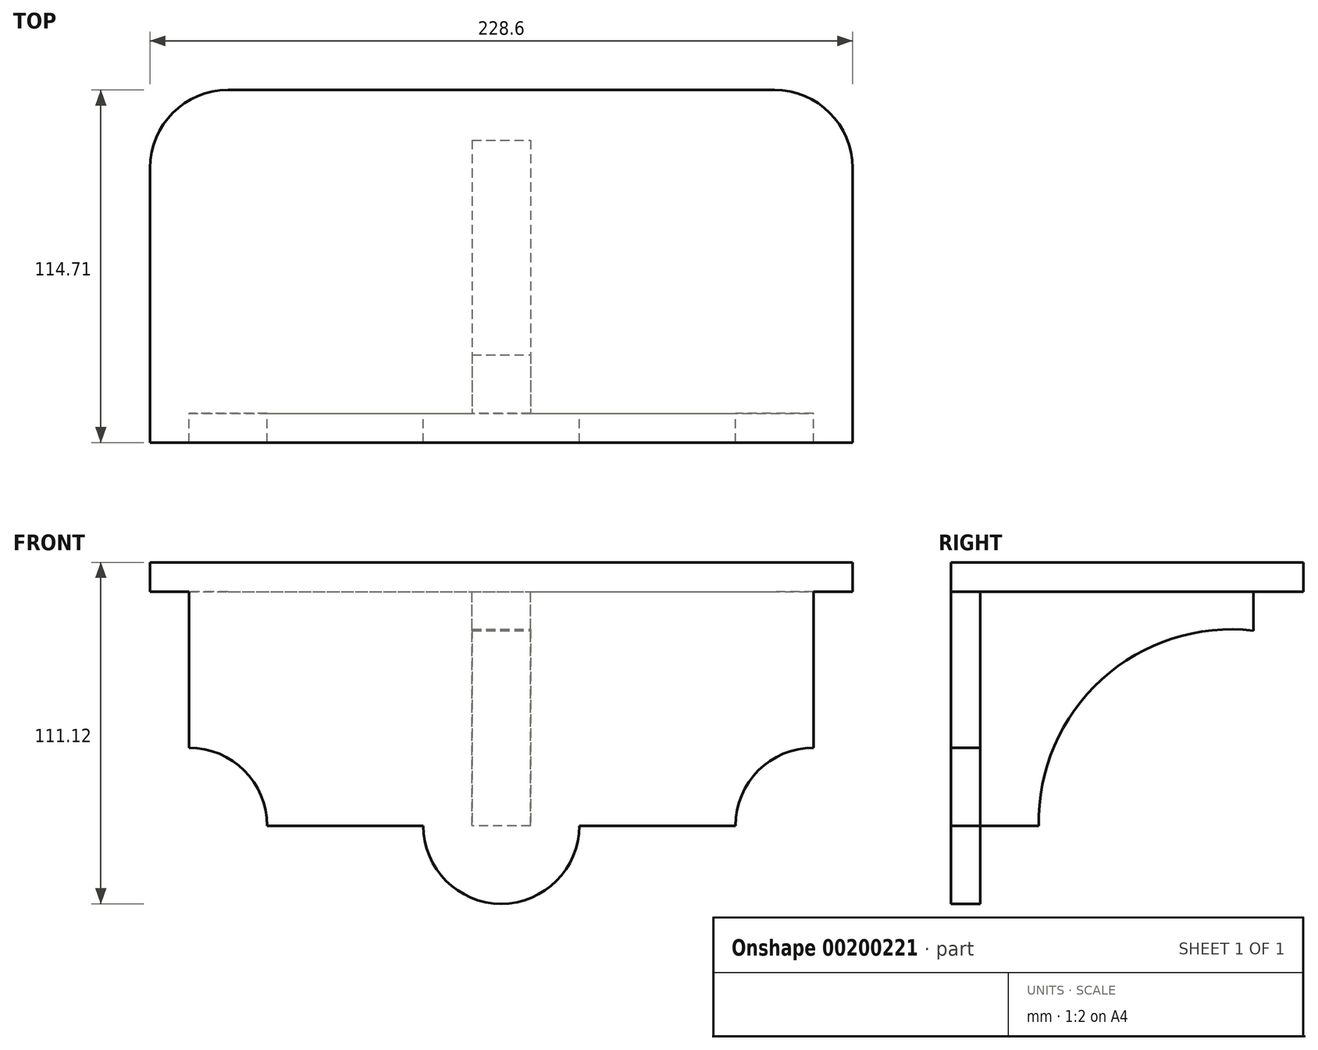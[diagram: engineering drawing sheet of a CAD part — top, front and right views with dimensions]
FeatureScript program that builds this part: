
annotation { "Feature Type Name" : "Feature", "Feature Type Description" : "" }
export const myFeature = defineFeature(function(context is Context, id is Id, definition is map)
    precondition{}
    {
        {
            var Q0;
            Q0=qCreatedBy(makeId("Front.planeOp"),FACE);
            var sketch = newSketch(context, id + "F0", { "sketchPlane" : qUnion([Q0])});
            skLineSegment(sketch, "E0", {"start": v(-62.52, 9.3) * mm, "end": v(140.68, 9.3) * mm});
            skLineSegment(sketch, "E1", {"start": v(-62.52, 9.3) * mm, "end": v(-62.52, -41.5) * mm});
            skLineSegment(sketch, "E2", {"start": v(140.68, 9.3) * mm, "end": v(140.68, -41.5) * mm});
            skLineSegment(sketch, "E3", {"start": v(-37.12, -66.9) * mm, "end": v(13.68, -66.9) * mm});
            skArc(sketch, "E4", {"start": v(-37.12, -66.9) * mm, "mid": v(-44.56, -48.94) * mm, "end": v(-62.52, -41.5) * mm});
            skArc(sketch, "E5", {"start": v(140.68, -41.5) * mm, "mid": v(122.72, -48.94) * mm, "end": v(115.28, -66.9) * mm});
            skArc(sketch, "E6", {"start": v(13.68, -66.9) * mm, "mid": v(39.08, -92.3) * mm, "end": v(64.48, -66.9) * mm});
            skLineSegment(sketch, "E7", {"start": v(64.48, -66.9) * mm, "end": v(115.28, -66.9) * mm});
            skSolve(sketch);
        }
        {
            var Q0;
            Q0 = qSketchRegion(id + "F0", true);
            extrude(context, id + "F1", {"entities" : qUnion([Q0]), "depth" : 9.52 * mm});
        }
        {
            var Q0;
            Q0=makeQuery(id+"F1.opExtrude","SWEPT_FACE",FACE,{"disambiguationData":[OSD([sQuery(id+"F0.wireOp",EDGE,"E0")])]});
            var sketch = newSketch(context, id + "F2", { "sketchPlane" : qUnion([Q0])});
            skLineSegment(sketch, "E8", {"start": v(-62.52, -9.53) * mm, "end": v(140.68, -9.53) * mm});
            skLineSegment(sketch, "E9", {"start": v(-62.52, -9.53) * mm, "end": v(-75.22, -9.53) * mm});
            skLineSegment(sketch, "E10", {"start": v(-75.22, -9.53) * mm, "end": v(-75.22, 79.78) * mm});
            skLineSegment(sketch, "E11", {"start": v(-49.82, 105.18) * mm, "end": v(127.98, 105.18) * mm});
            skLineSegment(sketch, "E12", {"start": v(153.38, 79.78) * mm, "end": v(153.38, -9.52) * mm});
            skLineSegment(sketch, "E13", {"start": v(153.38, -9.53) * mm, "end": v(140.68, -9.53) * mm});
            skArc(sketch, "E14", {"start": v(-49.82, 105.18) * mm, "mid": v(-67.78, 97.74) * mm, "end": v(-75.22, 79.78) * mm});
            skArc(sketch, "E15.MirrorC", {"start": v(127.98, 105.18) * mm, "mid": v(145.94, 97.74) * mm, "end": v(153.38, 79.78) * mm});
            skSolve(sketch);
        }
        {
            var Q0;
            Q0=makeQuery(id+"F2.imprint","IMPRINT",FACE,{"disambiguationData":[TD([[makeQuery(id+"F2.imprint","IMPRINT",EDGE,{"derivedFrom":sQuery(id+"F2.wireOp",EDGE,"E8")}),1.0]])]});
            var Q1;
            Q1=makeQuery(id+"F2.imprint","IMPRINT",FACE,{"disambiguationData":[TD([[makeQuery(id+"F2.imprint","IMPRINT",EDGE,{"derivedFrom":sQuery(id+"F2.wireOp",EDGE,"E9")}),-1.0]])]});
            extrude(context, id + "F3", {"entities" : qUnion([Q0, Q1]), "operationType" : NewBodyOperationType.ADD, "depth" : 9.52 * mm});
        }
        {
            var Q0;
            Q0=makeQuery(id+"F1.opExtrude","CAP_FACE",FACE,{"disambiguationData":[OSD([sQuery(id+"F0.wireOp",EDGE,"E0"),sQuery(id+"F0.wireOp",EDGE,"E1"),sQuery(id+"F0.wireOp",EDGE,"E2"),sQuery(id+"F0.wireOp",EDGE,"E3"),sQuery(id+"F0.wireOp",EDGE,"E4"),sQuery(id+"F0.wireOp",EDGE,"E5"),sQuery(id+"F0.wireOp",EDGE,"E6"),sQuery(id+"F0.wireOp",EDGE,"E7")])],"isStart":true});
            var sketch = newSketch(context, id + "F4", { "sketchPlane" : qUnion([Q0])});
            skLineSegment(sketch, "E16", {"start": v(62.52, -66.9) * mm, "end": v(63.15, -67.96) * mm});
            skLineSegment(sketch, "E17", {"start": v(-140.68, -66.9) * mm, "end": v(-48.6, -66.9) * mm});
            skLineSegment(sketch, "E18", {"start": v(62.52, -66.9) * mm, "end": v(-29.56, -66.9) * mm});
            skLineSegment(sketch, "E19", {"start": v(-48.6, -66.9) * mm, "end": v(-48.6, 9.3) * mm});
            skLineSegment(sketch, "E20", {"start": v(-29.56, -66.9) * mm, "end": v(-29.56, 9.3) * mm});
            skLineSegment(sketch, "E21", {"start": v(-48.6, 9.3) * mm, "end": v(-29.56, 9.3) * mm});
            skLineSegment(sketch, "E22", {"start": v(-48.6, -66.9) * mm, "end": v(-29.56, -66.9) * mm});
            skSolve(sketch);
        }
        {
            var Q0;
            Q0=makeQuery(id+"F4.imprint","IMPRINT",FACE,{"disambiguationData":[TD([[makeQuery(id+"F4.imprint","IMPRINT",EDGE,{"derivedFrom":sQuery(id+"F4.wireOp",EDGE,"E19")}),-1.0]])]});
            extrude(context, id + "F5", {"entities" : qUnion([Q0]), "operationType" : NewBodyOperationType.ADD, "depth" : 88.9 * mm});
        }
        {
            var Q0;
            Q0=makeQuery(id+"F5.opExtrude","SWEPT_FACE",FACE,{"disambiguationData":[OSD([sQuery(id+"F4.wireOp",EDGE,"E19")])]});
            var sketch = newSketch(context, id + "F6", { "sketchPlane" : qUnion([Q0])});
            skLineSegment(sketch, "E23", {"start": v(88.9, 9.3) * mm, "end": v(88.9, -3.4) * mm});
            skLineSegment(sketch, "E24", {"start": v(0, -66.9) * mm, "end": v(19.05, -66.9) * mm});
            skCircle(sketch, "E25", {"center": v(81.72, -65.67) * mm, "radius": 62.69 * mm});
            skPoint(sketch, "E25.third.point", {"position": v(132.14, -102.92) * mm});
            skSolve(sketch);
        }
        {
            var Q0;
            Q0 = qSketchRegion(id + "F6", true);
            extrude(context, id + "F7", {"entities" : qUnion([Q0]), "operationType" : NewBodyOperationType.REMOVE, "endBound" : BoundingType.THROUGH_ALL, "oppositeDirection" : true, "depth" : 25.4 * mm});
        }
    });
